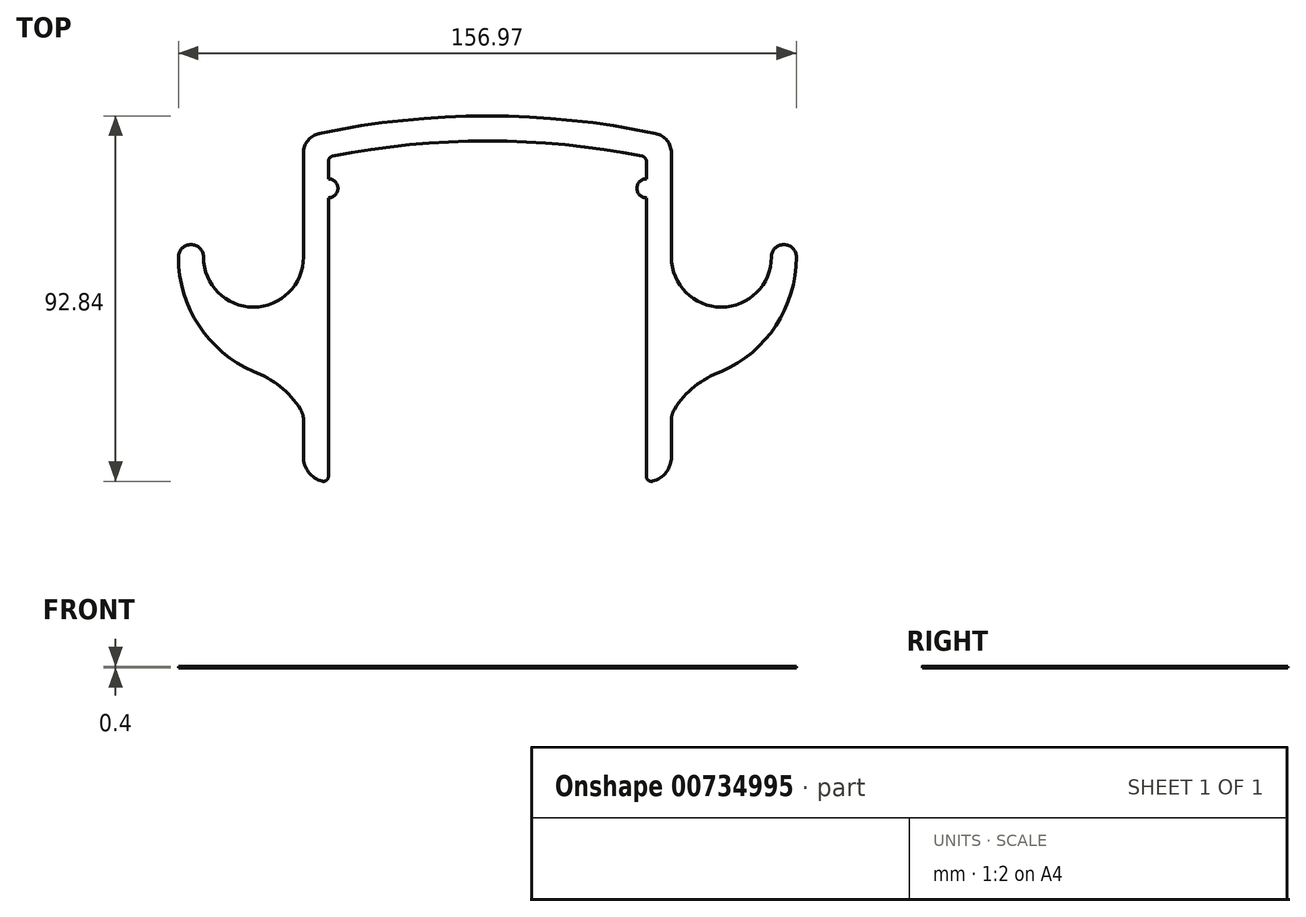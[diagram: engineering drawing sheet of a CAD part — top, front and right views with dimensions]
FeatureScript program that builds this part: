
annotation { "Feature Type Name" : "Feature", "Feature Type Description" : "" }
export const myFeature = defineFeature(function(context is Context, id is Id, definition is map)
    precondition{}
    {
        {
            assignVariable(context, id + "F0", {"name" : "THICKNESS", "anyValue" : .4});
        }
        {
            var Q0;
            Q0=qCreatedBy(makeId("Top.planeOp"),FACE);
            var sketch = newSketch(context, id + "F1", { "sketchPlane" : qUnion([Q0])});
            skLineSegment(sketch, "E0", {"start": v(0, -76.2) * mm, "end": v(0, 0) * mm});
            skLineSegment(sketch, "E1", {"start": v(-40.39, -196.85) * mm, "end": v(-40.39, 86.17) * mm, "construction": true});
            skLineSegment(sketch, "E2", {"start": v(-91.82, -127) * mm, "end": v(27.39, -127) * mm, "construction": true});
            skLineSegment(sketch, "E3", {"start": v(-88, 4.2) * mm, "end": v(8.84, 4.2) * mm, "construction": true});
            skArc(sketch, "E4", {"start": v(0, 0) * mm, "mid": v(-20.09, 3.07) * mm, "end": v(-40.39, 4.1) * mm});
            skArc(sketch, "E5.MirrorCS", {"start": v(-80.77, 0) * mm, "mid": v(-60.68, 3.07) * mm, "end": v(-40.39, 4.1) * mm});
            skLineSegment(sketch, "E6.MirrorCS", {"start": v(-80.77, -76.2) * mm, "end": v(-80.77, 0) * mm});
            skLineSegment(sketch, "E7.0", {"start": v(-87.12, -76.2) * mm, "end": v(-87.12, 5.11) * mm});
            skArc(sketch, "E7.1", {"start": v(-87.12, 5.11) * mm, "mid": v(-63.9, 9.11) * mm, "end": v(-40.39, 10.45) * mm});
            skArc(sketch, "E7.2", {"start": v(6.35, 5.11) * mm, "mid": v(-16.87, 9.11) * mm, "end": v(-40.39, 10.45) * mm});
            skLineSegment(sketch, "E7.3", {"start": v(6.35, -76.2) * mm, "end": v(6.35, 5.11) * mm});
            skArc(sketch, "E8", {"start": v(6.35, -76.2) * mm, "mid": v(4.5, -80.7) * mm, "end": v(0, -82.55) * mm});
            skLineSegment(sketch, "E9", {"start": v(0, -76.2) * mm, "end": v(0, -82.55) * mm});
            skLineSegment(sketch, "E10.MirrorCS", {"start": v(-80.77, -76.2) * mm, "end": v(-80.77, -82.55) * mm});
            skArc(sketch, "E11.MirrorCS", {"start": v(-87.12, -76.2) * mm, "mid": v(-85.26, -80.7) * mm, "end": v(-80.77, -82.55) * mm});
            skSolve(sketch);
        }
        {
            var Q0;
            Q0=qSketchRegion(id+"F1",true);
            var Q1;
            Q1=qSketchRegion(id+"F3",true);
            extrude(context, id + "F2", {"entities" : qUnion([Q0, Q1]), "depth" : (getVariable(context, 'THICKNESS')) * mm, "offsetDistance" : 25.4 * mm});
        }
        {
            var Q0;
            Q0=qCreatedBy(makeId("Top.planeOp"),FACE);
            var sketch = newSketch(context, id + "F3", { "sketchPlane" : qUnion([Q0])});
            skCircle(sketch, "E12", {"center": v(0, -7.94) * mm, "radius": 2.41 * mm});
            skCircle(sketch, "E13.MirrorC", {"center": v(-80.77, -7.94) * mm, "radius": 2.41 * mm});
            skSolve(sketch);
        }
        {
            var Q0;
            Q0=qSketchRegion(id+"F3",true);
            extrude(context, id + "F4", {"entities" : qUnion([Q0]), "operationType" : NewBodyOperationType.ADD, "depth" : (getVariable(context, 'THICKNESS')) * mm, "offsetDistance" : 25.4 * mm});
        }
        {
            var Q0;
            Q0=makeQuery(id+"F2.opExtrude","SWEPT_EDGE",EDGE,{"disambiguationData":[OSD([sQuery(id+"F1.wireOp",EDGE,"E7.0"),sQuery(id+"F1.wireOp",EDGE,"E7.1")])]});
            var Q1;
            Q1=makeQuery(id+"F2.opExtrude","SWEPT_EDGE",EDGE,{"disambiguationData":[OSD([sQuery(id+"F1.wireOp",EDGE,"E7.2"),sQuery(id+"F1.wireOp",EDGE,"E7.3")])]});
            fillet(context, id + "F5", {"entities" : qUnion([Q0, Q1]), "radius" : 5.08 * mm, "tangentPropagation" : true, "allowEdgeOverflow" : false});
        }
        {
            var Q0;
            Q0=makeQuery(id+"F2.opExtrude","SWEPT_EDGE",EDGE,{"disambiguationData":[OSD([sQuery(id+"F1.wireOp",EDGE,"E8"),sQuery(id+"F1.wireOp",EDGE,"E9")])]});
            var Q1;
            Q1=makeQuery(id+"F2.opExtrude","SWEPT_EDGE",EDGE,{"disambiguationData":[OSD([sQuery(id+"F1.wireOp",EDGE,"E10.MirrorCS"),sQuery(id+"F1.wireOp",EDGE,"E11.MirrorCS")])]});
            var Q2;
            Q2=makeQuery(id+"F2.opExtrude","SWEPT_EDGE",EDGE,{"disambiguationData":[OSD([sQuery(id+"F1.wireOp",EDGE,"E0"),sQuery(id+"F1.wireOp",EDGE,"E4")])]});
            var Q3;
            Q3=makeQuery(id+"F2.opExtrude","SWEPT_EDGE",EDGE,{"disambiguationData":[OSD([sQuery(id+"F1.wireOp",EDGE,"E5.MirrorCS"),sQuery(id+"F1.wireOp",EDGE,"E6.MirrorCS")])]});
            fillet(context, id + "F6", {"entities" : qUnion([Q0, Q1, Q2, Q3]), "radius" : 1.27 * mm, "tangentPropagation" : true, "allowEdgeOverflow" : false});
        }
        {
            var Q0;
            Q0=qCreatedBy(makeId("Top.planeOp"),FACE);
            var sketch = newSketch(context, id + "F7", { "sketchPlane" : qUnion([Q0])});
            skArc(sketch, "E14", {"start": v(6.35, -25.4) * mm, "mid": v(19.05, -38.1) * mm, "end": v(31.75, -25.4) * mm});
            skLineSegment(sketch, "E15", {"start": v(-17.7, -25.4) * mm, "end": v(46.73, -25.4) * mm, "construction": true});
            skCircle(sketch, "E16", {"center": v(34.92, -25.4) * mm, "radius": 3.18 * mm});
            skLineSegment(sketch, "E17", {"start": v(19.05, -25.4) * mm, "end": v(19.05, -101.6) * mm, "construction": true});
            skLineSegment(sketch, "E18", {"start": v(26.67, -25.4) * mm, "end": v(26.67, -101.6) * mm, "construction": true});
            skArc(sketch, "E19", {"start": v(38.1, -25.4) * mm, "mid": v(32.91, -42.8) * mm, "end": v(19.05, -54.5) * mm});
            skArc(sketch, "E20", {"start": v(19.05, -54.5) * mm, "mid": v(11.67, -58.77) * mm, "end": v(6.35, -65.43) * mm});
            skLineSegment(sketch, "E21", {"start": v(6.35, -25.4) * mm, "end": v(6.35, -65.43) * mm});
            skArc(sketch, "E22.MirrorCS", {"start": v(-87.12, -25.4) * mm, "mid": v(-99.82, -38.1) * mm, "end": v(-112.52, -25.4) * mm});
            skCircle(sketch, "E23.MirrorC", {"center": v(-115.7, -25.4) * mm, "radius": 3.18 * mm});
            skArc(sketch, "E24.MirrorCS", {"start": v(-118.87, -25.4) * mm, "mid": v(-113.69, -42.8) * mm, "end": v(-99.82, -54.5) * mm});
            skArc(sketch, "E25.MirrorCS", {"start": v(-99.82, -54.5) * mm, "mid": v(-92.44, -58.77) * mm, "end": v(-87.12, -65.43) * mm});
            skLineSegment(sketch, "E26.MirrorCS", {"start": v(-87.12, -25.4) * mm, "end": v(-87.12, -65.43) * mm});
            skSolve(sketch);
        }
        {
            var Q0;
            Q0=qSketchRegion(id+"F7",true);
            extrude(context, id + "F8", {"entities" : qUnion([Q0]), "operationType" : NewBodyOperationType.ADD, "depth" : (getVariable(context, 'THICKNESS')) * mm, "offsetDistance" : 25.4 * mm});
        }
        {
            var Q0;
            Q0=makeQuery(id+"F8.opExtrude","SWEPT_EDGE",EDGE,{"disambiguationData":[OSD([sQuery(id+"F7.wireOp",EDGE,"E20"),sQuery(id+"F7.wireOp",EDGE,"E21")])]});
            var Q1;
            Q1=makeQuery(id+"F8.opExtrude","SWEPT_EDGE",EDGE,{"disambiguationData":[OSD([sQuery(id+"F7.wireOp",EDGE,"E25.MirrorCS"),sQuery(id+"F7.wireOp",EDGE,"E26.MirrorCS")])]});
            fillet(context, id + "F9", {"entities" : qUnion([Q0, Q1]), "radius" : 5.08 * mm, "tangentPropagation" : true, "allowEdgeOverflow" : false});
        }
    });
